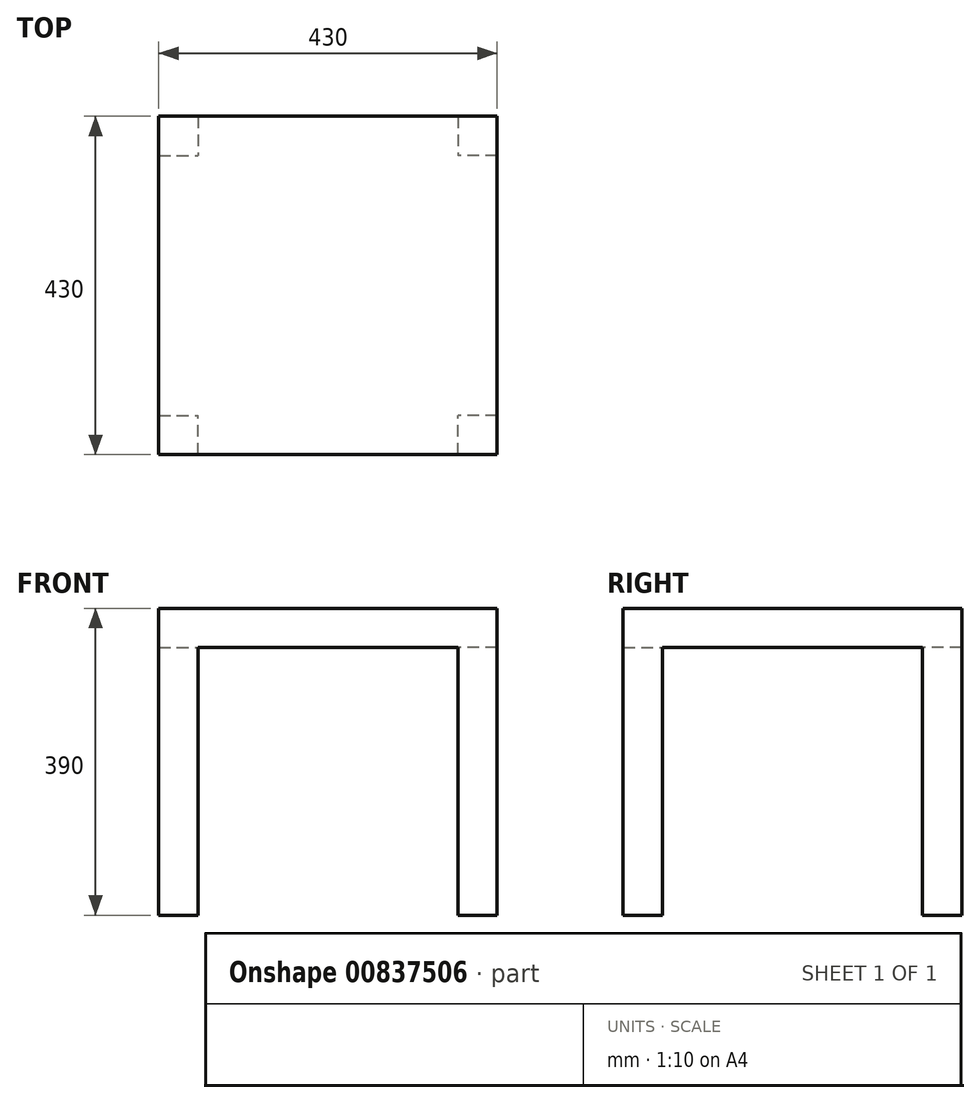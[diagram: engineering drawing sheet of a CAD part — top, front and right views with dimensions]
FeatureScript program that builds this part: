
annotation { "Feature Type Name" : "Feature", "Feature Type Description" : "" }
export const myFeature = defineFeature(function(context is Context, id is Id, definition is map)
    precondition{}
    {
        {
            var Q0;
            Q0=qCreatedBy(makeId("Top.planeOp"),FACE);
            cPlane(context, id + "F0", {"entities" : qUnion([Q0]), "cplaneType" : CPlaneType.OFFSET, "offset" : 390 * mm, "width" : 150 * mm, "height" : 150 * mm});
        }
        {
            var Q0;
            Q0=qCreatedBy(id+"F0.planeOp",FACE);
            var sketch = newSketch(context, id + "F1", { "sketchPlane" : qUnion([Q0])});
            skLineSegment(sketch, "E0.bottom", {"start": v(-215, 215) * mm, "end": v(215, 215) * mm});
            skLineSegment(sketch, "E0.top", {"start": v(-215, -215) * mm, "end": v(215, -215) * mm});
            skLineSegment(sketch, "E0.left", {"start": v(-215, 215) * mm, "end": v(-215, -215) * mm});
            skLineSegment(sketch, "E0.right", {"start": v(215, 215) * mm, "end": v(215, -215) * mm});
            skPoint(sketch, "E0.middle", {"position": v(0, 0) * mm});
            skSolve(sketch);
        }
        {
            var Q0;
            Q0=makeQuery(id+"F1.imprint","IMPRINT",FACE,{"disambiguationData":[TD([[makeQuery(id+"F1.imprint","IMPRINT",EDGE,{"derivedFrom":sQuery(id+"F1.wireOp",EDGE,"E0.bottom")}),-1.0]])]});
            extrude(context, id + "F2", {"entities" : qUnion([Q0]), "oppositeDirection" : true, "depth" : 50 * mm, "offsetDistance" : 25 * mm});
        }
        {
            var Q0;
            Q0=makeQuery(id+"F2.opExtrude","CAP_FACE",FACE,{"disambiguationData":[OSD([sQuery(id+"F1.wireOp",EDGE,"E0.bottom"),sQuery(id+"F1.wireOp",EDGE,"E0.top"),sQuery(id+"F1.wireOp",EDGE,"E0.left"),sQuery(id+"F1.wireOp",EDGE,"E0.right")])],"isStart":false});
            var sketch = newSketch(context, id + "F3", { "sketchPlane" : qUnion([Q0])});
            skLineSegment(sketch, "E1.bottom", {"start": v(215, 215) * mm, "end": v(165, 215) * mm});
            skLineSegment(sketch, "E1.top", {"start": v(215, 165) * mm, "end": v(165, 165) * mm});
            skLineSegment(sketch, "E1.left", {"start": v(215, 215) * mm, "end": v(215, 165) * mm});
            skLineSegment(sketch, "E1.right", {"start": v(165, 215) * mm, "end": v(165, 165) * mm});
            skLineSegment(sketch, "E2.bottom", {"start": v(-215, -215) * mm, "end": v(-165, -215) * mm});
            skLineSegment(sketch, "E2.top", {"start": v(-215, -165) * mm, "end": v(-165, -165) * mm});
            skLineSegment(sketch, "E2.left", {"start": v(-215, -215) * mm, "end": v(-215, -165) * mm});
            skLineSegment(sketch, "E2.right", {"start": v(-165, -215) * mm, "end": v(-165, -165) * mm});
            skLineSegment(sketch, "E3.bottom", {"start": v(215, -215) * mm, "end": v(165, -215) * mm});
            skLineSegment(sketch, "E3.top", {"start": v(215, -165) * mm, "end": v(165, -165) * mm});
            skLineSegment(sketch, "E3.left", {"start": v(215, -215) * mm, "end": v(215, -165) * mm});
            skLineSegment(sketch, "E3.right", {"start": v(165, -215) * mm, "end": v(165, -165) * mm});
            skLineSegment(sketch, "E4.bottom", {"start": v(-215, 215) * mm, "end": v(-165, 215) * mm});
            skLineSegment(sketch, "E4.top", {"start": v(-215, 165) * mm, "end": v(-165, 165) * mm});
            skLineSegment(sketch, "E4.left", {"start": v(-215, 215) * mm, "end": v(-215, 165) * mm});
            skLineSegment(sketch, "E4.right", {"start": v(-165, 215) * mm, "end": v(-165, 165) * mm});
            skSolve(sketch);
        }
        {
            var Q0;
            Q0=makeQuery(id+"F3.imprint","IMPRINT",FACE,{"disambiguationData":[TD([[makeQuery(id+"F3.imprint","IMPRINT",EDGE,{"derivedFrom":sQuery(id+"F3.wireOp",EDGE,"E1.bottom")}),-1.0]])]});
            var Q1;
            Q1=makeQuery(id+"F3.imprint","IMPRINT",FACE,{"disambiguationData":[TD([[makeQuery(id+"F3.imprint","IMPRINT",EDGE,{"derivedFrom":sQuery(id+"F3.wireOp",EDGE,"E4.bottom")}),-1.0]])]});
            var Q2;
            Q2=makeQuery(id+"F3.imprint","IMPRINT",FACE,{"disambiguationData":[TD([[makeQuery(id+"F3.imprint","IMPRINT",EDGE,{"derivedFrom":sQuery(id+"F3.wireOp",EDGE,"E2.bottom")}),1.0]])]});
            var Q3;
            Q3=makeQuery(id+"F3.imprint","IMPRINT",FACE,{"disambiguationData":[TD([[makeQuery(id+"F3.imprint","IMPRINT",EDGE,{"derivedFrom":sQuery(id+"F3.wireOp",EDGE,"E3.bottom")}),1.0]])]});
            var Q4;
            Q4=qCreatedBy(makeId("Top.planeOp"),FACE);
            extrude(context, id + "F4", {"entities" : qUnion([Q0, Q1, Q2, Q3]), "operationType" : NewBodyOperationType.ADD, "endBound" : BoundingType.UP_TO_SURFACE, "depth" : 25 * mm, "endBoundEntityFace" : qUnion([Q4]), "offsetDistance" : 25 * mm});
        }
    });
